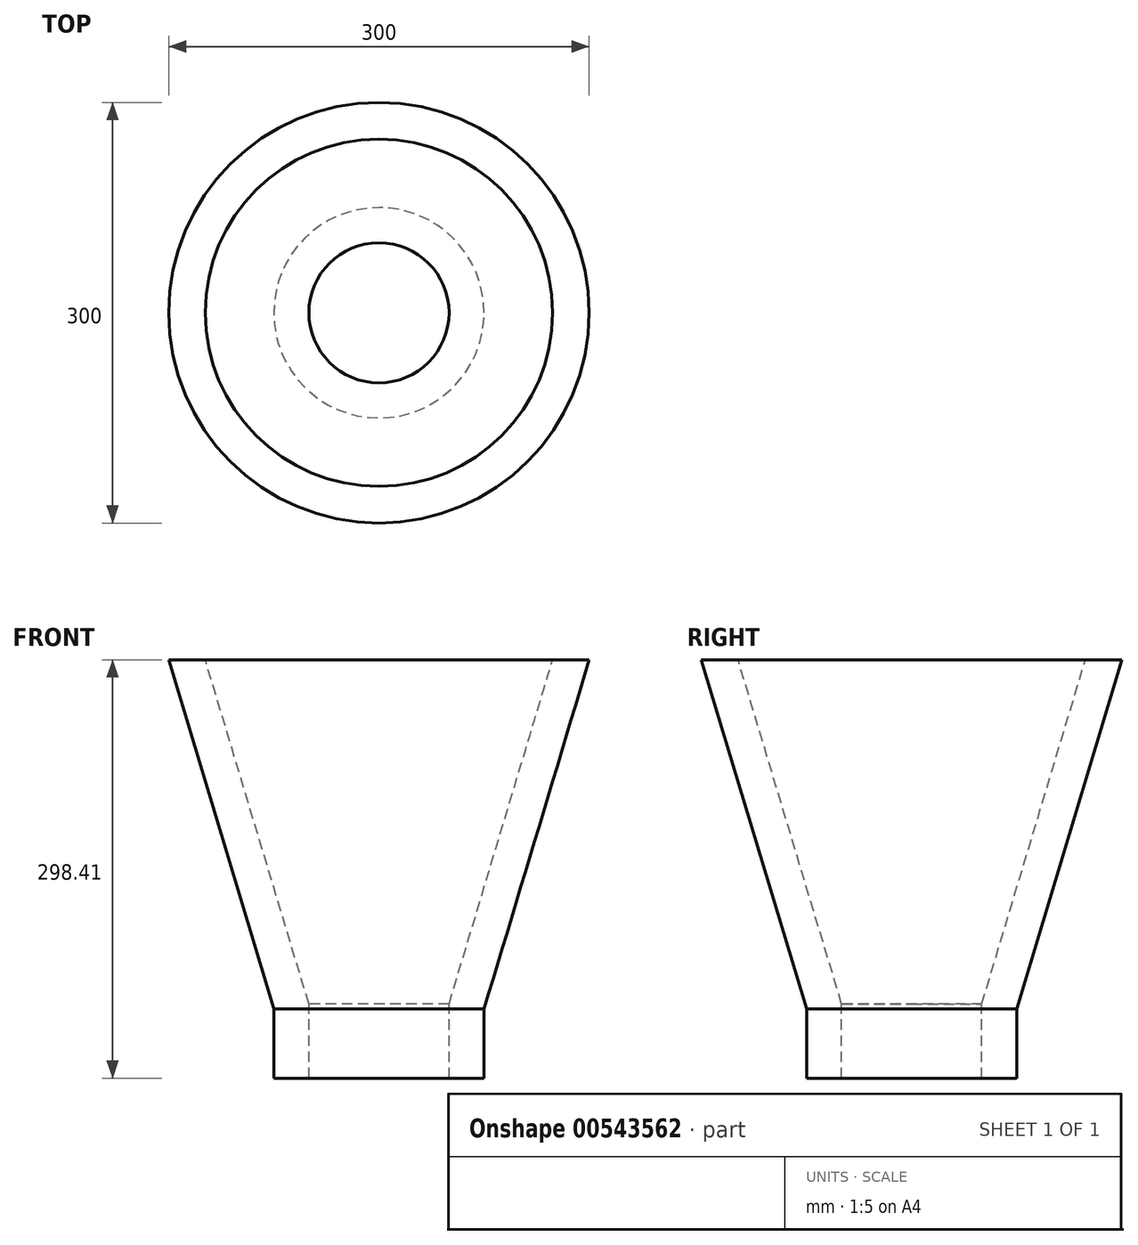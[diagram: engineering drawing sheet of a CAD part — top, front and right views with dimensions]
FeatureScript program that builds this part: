
annotation { "Feature Type Name" : "Feature", "Feature Type Description" : "" }
export const myFeature = defineFeature(function(context is Context, id is Id, definition is map)
    precondition{}
    {
        {
            var Q0;
            Q0=qCreatedBy(makeId("Front.planeOp"),FACE);
            var sketch = newSketch(context, id + "F0", { "sketchPlane" : qUnion([Q0])});
            skLineSegment(sketch, "E0", {"start": v(0, 154.7) * mm, "end": v(0, -143.96) * mm});
            skLineSegment(sketch, "E1", {"start": v(123.9, 154.7) * mm, "end": v(150, 154.7) * mm});
            skLineSegment(sketch, "E2", {"start": v(150, 154.7) * mm, "end": v(75, -94.42) * mm});
            skLineSegment(sketch, "E3", {"start": v(75, -94.42) * mm, "end": v(75, -143.72) * mm});
            skPoint(sketch, "E4.orphan", {"position": v(0, -94.42) * mm});
            skLineSegment(sketch, "E5", {"start": v(75, -143.72) * mm, "end": v(50, -143.72) * mm});
            skLineSegment(sketch, "E6.0", {"start": v(123.9, 154.7) * mm, "end": v(50, -90.74) * mm});
            skLineSegment(sketch, "E7.0", {"start": v(50, -90.74) * mm, "end": v(50, -143.72) * mm});
            skPoint(sketch, "E8.orphan", {"position": v(0, -143.72) * mm});
            skSolve(sketch);
        }
        {
            var Q0;
            Q0=makeQuery(id+"F0.imprint","IMPRINT",FACE,{"disambiguationData":[TD([[makeQuery(id+"F0.imprint","IMPRINT",EDGE,{"derivedFrom":sQuery(id+"F0.wireOp",EDGE,"E1")}),-1.0]])]});
            var Q1;
            Q1=sQuery(id+"F0.wireOp",EDGE,"E0");
            revolve(context, id + "F1", {"entities" : qUnion([Q0]), "axis" : qUnion([Q1]), "revolveType" : RevolveType.FULL});
        }
    });
